# Revit family: TESK_Насос вертикальный_SVM(T)-64
name_source: partatom
category: Оборудование
units: mm (PartAtom-declared; Revit-internal decimal feet)

## family parameters
Всегда вертикально = Да
Классификация = Насос
На основе рабочей плоскости = Нет
Общий = Нет
При загрузке вырезать с полостями = Нет
Размер круглого соединителя = Использовать диаметр
Тип детали = Вставляется
Точка расчета площади = Нет

## types (44) — shared parameters
ADSK_Версия Revit = 2019
ADSK_Версия семейства = 1.0
ADSK_Диаметр условный = 100 мм
ADSK_Единица измерения = шт.
ADSK_Завод-изготовитель = TESK
ADSK_Классификация нагрузок = Прочее
ADSK_Количество = 1
ADSK_Количество фаз = 3
ADSK_Количество фаз числовое = 3
ADSK_Коэффициент мощности = 1
ADSK_Наименование краткое = Вертикальный многоступенчатый центробежный насос
ADSK_Напряжение = 400 В
URL = www.teskpump.ru
Материал_1 = TESK_Черный_Условный
Материал_2 = TESK_Нержавеющая сталь
Материал_КорпусДвигателя = TESK_Черный_Ребра_Условный
Таблица_Поиска = TESK_SVM(T)-64
УГО_Длина = 365 мм
Фланец_Толщина = 26 мм

## per-type parameters (varying)
| type | ADSK_Код изделия | ADSK_Масса | ADSK_Масса_Текст | ADSK_Наименование | ADSK_Номинальная мощность | ADSK_Полная мощность | D_Башня | Высота_Башня | Высота_Корпуса | Двигатель_Высота | Двигатель_ОтступКоробки | Двигатель_Ширина | Материал_КорпусУлитка | Напор максимальный | Толщина_ФланцаДвигателя |
| SVM 64-1-1 4kW 3x380V 50Hz IE3 | 7764-10-10003380NSSF | 93 | 93 | Вертикальный многоступенчатый центробежный насос SVM, DN100, PN16, Hmax=19м (3x380V 50Hz IE3) | 4 кВт | 4 кВ·А | 173 мм | 200 мм | 561 мм | 370 мм | 188 мм | 230 мм | TESK_Нержавеющая сталь | 19 | 11 мм |
| SVM 64-1 5.5kW 3x380V 50Hz IE3 | 7764-100003380NSSF | 105 | 105 | Вертикальный многоступенчатый центробежный насос SVM, DN100, PN16, Hmax=27м (3x380V 50Hz IE3) | 6 кВт | 6 кВ·А | 195 мм | 200 мм | 561 мм | 435 мм | 208 мм | 260 мм | TESK_Нержавеющая сталь | 27 | 13 мм |
| SVM 64-2-2 7.5kW 3x380V 50Hz IE3 | 7764-20-20003380NSSF | 110 | 110 | Вертикальный многоступенчатый центробежный насос SVM, DN100, PN16, Hmax=39м (3x380V 50Hz IE3) | 8 кВт | 8 кВ·А | 195 мм | 220 мм | 644 мм | 435 мм | 208 мм | 260 мм | TESK_Нержавеющая сталь | 39 | 13 мм |
| SVM 64-2-1 11kW 3x380V 50Hz IE3 | 7764-20-10003380NSSF | 182 | 182 | Вертикальный многоступенчатый центробежный насос SVM, DN100, PN16, Hmax=46м (3x380V 50Hz IE3) | 11 кВт | 11 кВ·А | 263 мм | 240 мм | 754 мм | 580 мм | 260 мм | 350 мм | TESK_Нержавеющая сталь | 46 | 17 мм |
| SVM 64-2 11kW 3x380V 50Hz IE3 | 7764-200003380NSSF | 182 | 182 | Вертикальный многоступенчатый центробежный насос SVM, DN100, PN16, Hmax=53м (3x380V 50Hz IE3) | 11 кВт | 11 кВ·А | 263 мм | 240 мм | 754 мм | 580 мм | 260 мм | 350 мм | TESK_Нержавеющая сталь | 53 | 17 мм |
| SVM 64-3- 15kW 3x380V 50Hz IE3 | 7764-30-20003380NSSF | 197 | 197 | Вертикальный многоступенчатый центробежный насос SVM, DN100, PN16, Hmax=66м (3x380V 50Hz IE3) | 15 кВт | 15 кВ·А | 263 мм | 260 мм | 836 мм | 580 мм | 260 мм | 350 мм | TESK_Нержавеющая сталь | 66 | 17 мм |
| SVM 64-3-2 15kW 3x380V 50Hz IE3 | 7764-30-10003380NSSF | 197 | 197 | Вертикальный многоступенчатый центробежный насос SVM, DN100, PN16, Hmax=73м (3x380V 50Hz IE3) | 15 кВт | 15 кВ·А | 263 мм | 260 мм | 836 мм | 580 мм | 260 мм | 350 мм | TESK_Нержавеющая сталь | 73 | 17 мм |
| SVM 64-3 18.5kW 3x380V 50Hz IE3 | 7764-300003380NSSF | 221 | 221 | Вертикальный многоступенчатый центробежный насос SVM, DN100, PN16, Hmax=80м (3x380V 50Hz IE3) | 19 кВт | 19 кВ·А | 248 мм | 260 мм | 836 мм | 610 мм | 260 мм | 330 мм | TESK_Нержавеющая сталь | 80 | 18 мм |
| SVM 64-4-2 18.5kW 3x380V 50Hz IE3 | 7764-40-20003380NSSF | 225 | 225 | Вертикальный многоступенчатый центробежный насос SVM, DN100, PN16, Hmax=92м (3x380V 50Hz IE3) | 19 кВт | 19 кВ·А | 263 мм | 300 мм | 919 мм | 610 мм | 260 мм | 350 мм | TESK_Нержавеющая сталь | 92 | 18 мм |
| SVM 64-4-1 22kW 3x380V 50Hz IE3 | 7764-40-10003380NSSF | 258 | 258 | Вертикальный многоступенчатый центробежный насос SVM, DN100, PN16, Hmax=100м (3x380V 50Hz IE3) | 22 кВт | 22 кВ·А | 270 мм | 300 мм | 919 мм | 645 мм | 285 мм | 360 мм | TESK_Нержавеющая сталь | 100 | 19 мм |
| SVM 64-4 22kW 3x380V 50Hz IE3 | 7764-400003380NSSF | 258 | 258 | Вертикальный многоступенчатый центробежный насос SVM, DN100, PN16, Hmax=107м (3x380V 50Hz IE3) | 22 кВт | 22 кВ·А | 270 мм | 300 мм | 919 мм | 645 мм | 285 мм | 360 мм | TESK_Нержавеющая сталь | 107 | 19 мм |
| SVM 64-5-2 30kW 3x380V 50Hz IE3 | 7764-50-20003380NSSF | 317 | 317 | Вертикальный многоступенчатый центробежный насос SVM, DN100, PN16, Hmax=121м (3x380V 50Hz IE3) | 30 кВт | 30 кВ·А | 300 мм | 320 мм | 1001 мм | 705 мм | 310 мм | 400 мм | TESK_Нержавеющая сталь | 121 | 21 мм |
| SVM 64-5-1 30kW 3x380V 50Hz IE3 | 7764-50-10003380NSSF | 321 | 321 | Вертикальный многоступенчатый центробежный насос SVM, DN100, PN16, Hmax=128м (3x380V 50Hz IE3) | 30 кВт | 30 кВ·А | 300 мм | 320 мм | 1001 мм | 705 мм | 310 мм | 400 мм | TESK_Нержавеющая сталь | 128 | 21 мм |
| SVM 64-5 30kW 3x380V 50Hz IE3 | 7764-500003380NSSF | 321 | 321 | Вертикальный многоступенчатый центробежный насос SVM, DN100, PN16, Hmax=136м (3x380V 50Hz IE3) | 30 кВт | 30 кВ·А | 300 мм | 320 мм | 1001 мм | 705 мм | 310 мм | 400 мм | TESK_Нержавеющая сталь | 136 | 21 мм |
| SVM 64-6-2 30kW 3x380V 50Hz IE3 | 7764-60-20003380NSSF | 325 | 325 | Вертикальный многоступенчатый центробежный насос SVM, DN100, PN16, Hmax=150м (3x380V 50Hz IE3) | 30 кВт | 30 кВ·А | 300 мм | 340 мм | 1084 мм | 705 мм | 310 мм | 400 мм | TESK_Нержавеющая сталь | 150 | 21 мм |
| SVM 64-6-1 37kW 3x380V 50Hz IE3 | 7764-60-10003380NSSF | 349 | 349 | Вертикальный многоступенчатый центробежный насос SVM, DN100, PN16, Hmax=157м (3x380V 50Hz IE3) | 37 кВт | 37 кВ·А | 300 мм | 340 мм | 1084 мм | 705 мм | 310 мм | 400 мм | TESK_Нержавеющая сталь | 157 | 21 мм |
| SVM 64-6 37kW 3x380V 50Hz IE3 | 7764-600003380NSSF | 349 | 349 | Вертикальный многоступенчатый центробежный насос SVM, DN100, PN16, Hmax=164м (3x380V 50Hz IE3) | 37 кВт | 37 кВ·А | 300 мм | 340 мм | 1084 мм | 705 мм | 310 мм | 400 мм | TESK_Нержавеющая сталь | 164 | 21 мм |
| SVM 64-7-2 37kW 3x380V 50Hz IE3 | 7764-70-20003380NSSF | 353 | 353 | Вертикальный многоступенчатый центробежный насос SVM, DN100, PN16, Hmax=179м (3x380V 50Hz IE3) | 37 кВт | 37 кВ·А | 300 мм | 380 мм | 1166 мм | 705 мм | 310 мм | 400 мм | TESK_Нержавеющая сталь | 179 | 21 мм |
| SVM 64-7-1 37kW 3x380V 50Hz IE3 | 7764-70-10003380NSSF | 353 | 353 | Вертикальный многоступенчатый центробежный насос SVM, DN100, PN16, Hmax=186м (3x380V 50Hz IE3) | 37 кВт | 37 кВ·А | 300 мм | 380 мм | 1166 мм | 705 мм | 310 мм | 400 мм | TESK_Нержавеющая сталь | 186 | 21 мм |
| SVM 64-7 45kW 3x380V 50Hz IE3 | 7764-700003380NSSF | 420 | 420 | Вертикальный многоступенчатый центробежный насос SVM, DN100, PN16, Hmax=193м (3x380V 50Hz IE3) | 45 кВт | 45 кВ·А | 345 мм | 380 мм | 1166 мм | 740 мм | 340 мм | 460 мм | TESK_Нержавеющая сталь | 193 | 22 мм |
| SVM 64-8-2 45kW 3x380V 50Hz IE3 | 7764-80-20003380NSSF | 424 | 424 | Вертикальный многоступенчатый центробежный насос SVM, DN100, PN16, Hmax=207м (3x380V 50Hz IE3) | 45 кВт | 45 кВ·А | 345 мм | 400 мм | 1248 мм | 740 мм | 340 мм | 460 мм | TESK_Нержавеющая сталь | 207 | 22 мм |
| SVM 64-8-1 45kW 3x380V 50Hz IE3 | 7764-80-10003380NSSF | 424 | 424 | Вертикальный многоступенчатый центробежный насос SVM, DN100, PN16, Hmax=215м (3x380V 50Hz IE3) | 45 кВт | 45 кВ·А | 345 мм | 400 мм | 1248 мм | 740 мм | 340 мм | 460 мм | TESK_Нержавеющая сталь | 215 | 22 мм |
| SVMT 64-1-1 4kW 3x380V 50Hz IE3 | 7764-10-10003380N | 93 | 93 | Вертикальный многоступенчатый центробежный насос SVMT, DN100, PN16, Hmax=19м (3x380V 50Hz IE3) | 4 кВт | 4 кВ·А | 173 мм | 200 мм | 561 мм | 370 мм | 188 мм | 230 мм | TESK_Черный_Условный | 19 | 11 мм |
| SVMT 64-1 5.5kW 3x380V 50Hz IE3 | 7764-100003380N | 105 | 105 | Вертикальный многоступенчатый центробежный насос SVMT, DN100, PN16, Hmax=27м (3x380V 50Hz IE3) | 6 кВт | 6 кВ·А | 195 мм | 200 мм | 561 мм | 435 мм | 208 мм | 260 мм | TESK_Черный_Условный | 27 | 13 мм |
| SVMT 64-2-2 7.5kW 3x380V 50Hz IE3 | 7764-20-20003380N | 110 | 110 | Вертикальный многоступенчатый центробежный насос SVMT, DN100, PN16, Hmax=39м (3x380V 50Hz IE3) | 8 кВт | 8 кВ·А | 195 мм | 220 мм | 644 мм | 435 мм | 208 мм | 260 мм | TESK_Черный_Условный | 39 | 13 мм |
| SVMT 64-2-1 11kW 3x380V 50Hz IE3 | 7764-20-10003380N | 182 | 182 | Вертикальный многоступенчатый центробежный насос SVMT, DN100, PN16, Hmax=46м (3x380V 50Hz IE3) | 11 кВт | 11 кВ·А | 263 мм | 240 мм | 754 мм | 580 мм | 260 мм | 350 мм | TESK_Черный_Условный | 46 | 17 мм |
| SVMT 64-2 11kW 3x380V 50Hz IE3 | 7764-200003380N | 182 | 182 | Вертикальный многоступенчатый центробежный насос SVMT, DN100, PN16, Hmax=53м (3x380V 50Hz IE3) | 11 кВт | 11 кВ·А | 263 мм | 240 мм | 754 мм | 580 мм | 260 мм | 350 мм | TESK_Черный_Условный | 53 | 17 мм |
| SVMT 64-3- 15kW 3x380V 50Hz IE3 | 7764-30-20003380N | 197 | 197 | Вертикальный многоступенчатый центробежный насос SVMT, DN100, PN16, Hmax=66м (3x380V 50Hz IE3) | 15 кВт | 15 кВ·А | 263 мм | 260 мм | 836 мм | 580 мм | 260 мм | 350 мм | TESK_Черный_Условный | 66 | 17 мм |
| SVMT 64-3-2 15kW 3x380V 50Hz IE3 | 7764-30-10003380N | 197 | 197 | Вертикальный многоступенчатый центробежный насос SVMT, DN100, PN16, Hmax=73м (3x380V 50Hz IE3) | 15 кВт | 15 кВ·А | 263 мм | 260 мм | 836 мм | 580 мм | 260 мм | 350 мм | TESK_Черный_Условный | 73 | 17 мм |
| SVMT 64-3 18.5kW 3x380V 50Hz IE3 | 7764-300003380N | 221 | 221 | Вертикальный многоступенчатый центробежный насос SVMT, DN100, PN16, Hmax=80м (3x380V 50Hz IE3) | 19 кВт | 19 кВ·А | 248 мм | 260 мм | 836 мм | 610 мм | 260 мм | 330 мм | TESK_Черный_Условный | 80 | 18 мм |
| SVMT 64-4-2 18.5kW 3x380V 50Hz IE3 | 7764-40-20003380N | 225 | 225 | Вертикальный многоступенчатый центробежный насос SVMT, DN100, PN16, Hmax=92м (3x380V 50Hz IE3) | 19 кВт | 19 кВ·А | 263 мм | 300 мм | 919 мм | 610 мм | 260 мм | 350 мм | TESK_Черный_Условный | 92 | 18 мм |
| SVMT 64-4-1 22kW 3x380V 50Hz IE3 | 7764-40-10003380N | 258 | 258 | Вертикальный многоступенчатый центробежный насос SVMT, DN100, PN16, Hmax=100м (3x380V 50Hz IE3) | 22 кВт | 22 кВ·А | 270 мм | 300 мм | 919 мм | 645 мм | 285 мм | 360 мм | TESK_Черный_Условный | 100 | 19 мм |
| SVMT 64-4 22kW 3x380V 50Hz IE3 | 7764-400003380N | 258 | 258 | Вертикальный многоступенчатый центробежный насос SVMT, DN100, PN16, Hmax=107м (3x380V 50Hz IE3) | 22 кВт | 22 кВ·А | 270 мм | 300 мм | 919 мм | 645 мм | 285 мм | 360 мм | TESK_Черный_Условный | 107 | 19 мм |
| SVMT 64-5-2 30kW 3x380V 50Hz IE3 | 7764-50-20003380N | 317 | 317 | Вертикальный многоступенчатый центробежный насос SVMT, DN100, PN16, Hmax=121м (3x380V 50Hz IE3) | 30 кВт | 30 кВ·А | 300 мм | 320 мм | 1001 мм | 705 мм | 310 мм | 400 мм | TESK_Черный_Условный | 121 | 21 мм |
| SVMT 64-5-1 30kW 3x380V 50Hz IE3 | 7764-50-10003380N | 321 | 321 | Вертикальный многоступенчатый центробежный насос SVMT, DN100, PN16, Hmax=128м (3x380V 50Hz IE3) | 30 кВт | 30 кВ·А | 300 мм | 320 мм | 1001 мм | 705 мм | 310 мм | 400 мм | TESK_Черный_Условный | 128 | 21 мм |
| SVMT 64-5 30kW 3x380V 50Hz IE3 | 7764-500003380N | 321 | 321 | Вертикальный многоступенчатый центробежный насос SVMT, DN100, PN16, Hmax=136м (3x380V 50Hz IE3) | 30 кВт | 30 кВ·А | 300 мм | 320 мм | 1001 мм | 705 мм | 310 мм | 400 мм | TESK_Черный_Условный | 136 | 21 мм |
| SVMT 64-6-2 30kW 3x380V 50Hz IE3 | 7764-60-20003380N | 325 | 325 | Вертикальный многоступенчатый центробежный насос SVMT, DN100, PN16, Hmax=150м (3x380V 50Hz IE3) | 30 кВт | 30 кВ·А | 300 мм | 340 мм | 1084 мм | 705 мм | 310 мм | 400 мм | TESK_Черный_Условный | 150 | 21 мм |
| SVMT 64-6-1 37kW 3x380V 50Hz IE3 | 7764-60-10003380N | 349 | 349 | Вертикальный многоступенчатый центробежный насос SVMT, DN100, PN16, Hmax=157м (3x380V 50Hz IE3) | 37 кВт | 37 кВ·А | 300 мм | 340 мм | 1084 мм | 705 мм | 310 мм | 400 мм | TESK_Черный_Условный | 157 | 21 мм |
| SVMT 64-6 37kW 3x380V 50Hz IE3 | 7764-600003380N | 349 | 349 | Вертикальный многоступенчатый центробежный насос SVMT, DN100, PN16, Hmax=164м (3x380V 50Hz IE3) | 37 кВт | 37 кВ·А | 300 мм | 340 мм | 1084 мм | 705 мм | 310 мм | 400 мм | TESK_Черный_Условный | 164 | 21 мм |
| SVMT 64-7-2 37kW 3x380V 50Hz IE3 | 7764-70-20003380N | 353 | 353 | Вертикальный многоступенчатый центробежный насос SVMT, DN100, PN16, Hmax=179м (3x380V 50Hz IE3) | 37 кВт | 37 кВ·А | 300 мм | 380 мм | 1166 мм | 705 мм | 310 мм | 400 мм | TESK_Черный_Условный | 179 | 21 мм |
| SVMT 64-7-1 37kW 3x380V 50Hz IE3 | 7764-70-10003380N | 353 | 353 | Вертикальный многоступенчатый центробежный насос SVMT, DN100, PN16, Hmax=186м (3x380V 50Hz IE3) | 37 кВт | 37 кВ·А | 300 мм | 380 мм | 1166 мм | 705 мм | 310 мм | 400 мм | TESK_Черный_Условный | 186 | 21 мм |
| SVMT 64-7 45kW 3x380V 50Hz IE3 | 7764-700003380N | 420 | 420 | Вертикальный многоступенчатый центробежный насос SVMT, DN100, PN16, Hmax=193м (3x380V 50Hz IE3) | 45 кВт | 45 кВ·А | 345 мм | 380 мм | 1166 мм | 740 мм | 340 мм | 460 мм | TESK_Черный_Условный | 193 | 22 мм |
| SVMT 64-8-2 45kW 3x380V 50Hz IE3 | 7764-80-20003380N | 424 | 424 | Вертикальный многоступенчатый центробежный насос SVMT, DN100, PN16, Hmax=207м (3x380V 50Hz IE3) | 45 кВт | 45 кВ·А | 345 мм | 400 мм | 1248 мм | 740 мм | 340 мм | 460 мм | TESK_Черный_Условный | 207 | 22 мм |
| SVMT 64-8-1 45kW 3x380V 50Hz IE3 | 7764-80-10003380N | 424 | 424 | Вертикальный многоступенчатый центробежный насос SVMT, DN100, PN16, Hmax=215м (3x380V 50Hz IE3) | 45 кВт | 45 кВ·А | 345 мм | 400 мм | 1248 мм | 740 мм | 340 мм | 460 мм | TESK_Черный_Условный | 215 | 22 мм |

note: column(s) folded — value = type name in every type: ADSK_Марка
